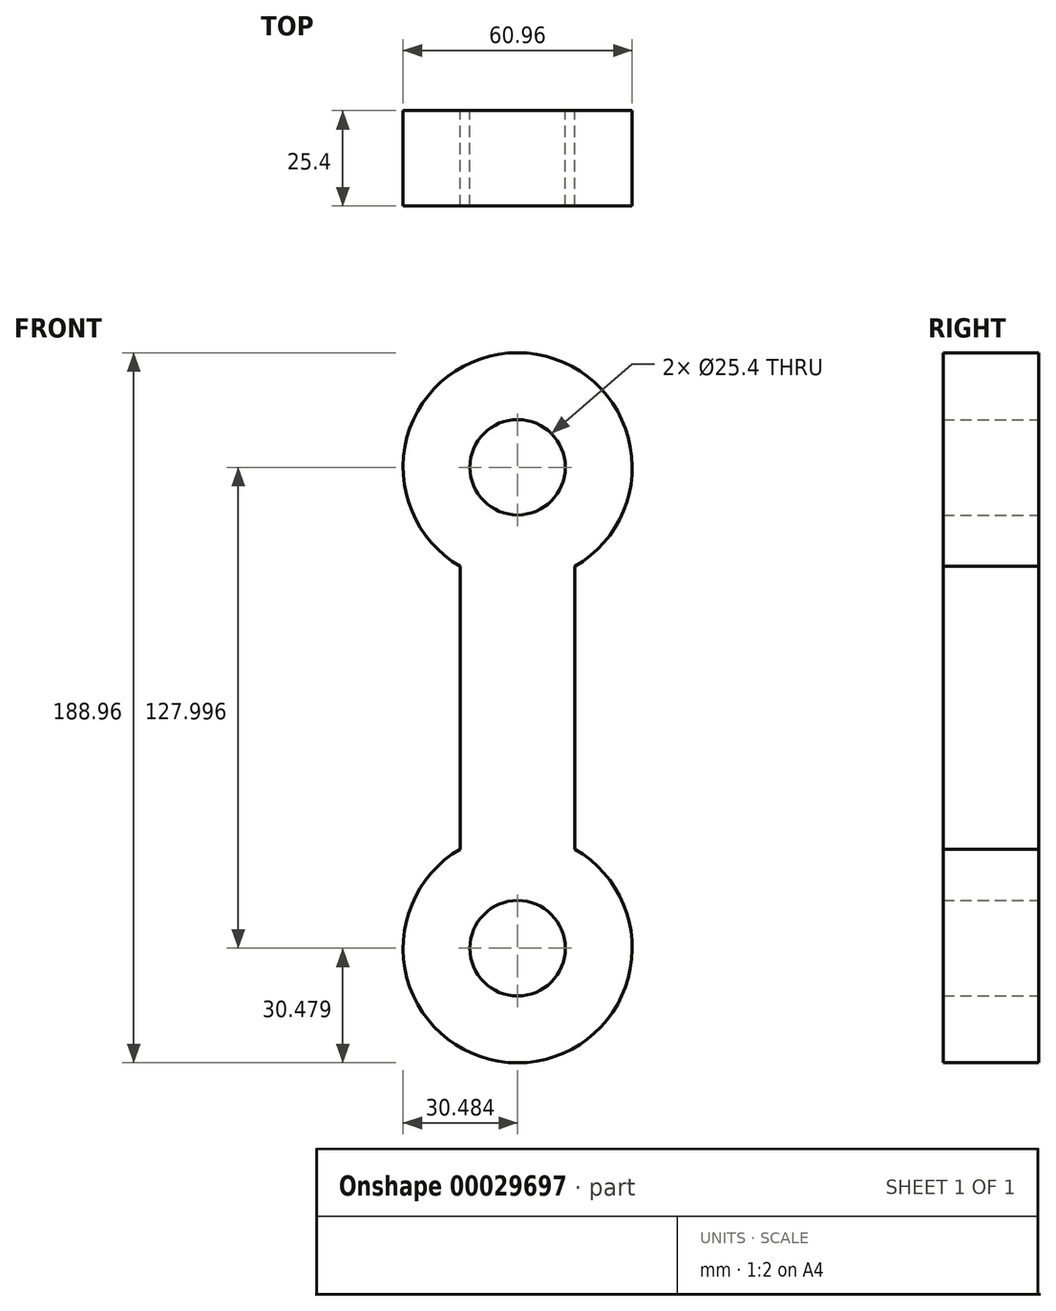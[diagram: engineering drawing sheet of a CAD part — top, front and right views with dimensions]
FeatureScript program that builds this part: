
annotation { "Feature Type Name" : "Feature", "Feature Type Description" : "" }
export const myFeature = defineFeature(function(context is Context, id is Id, definition is map)
    precondition{}
    {
        {
            var Q0;
            Q0=qCreatedBy(makeId("Front.planeOp"),FACE);
            var sketch = newSketch(context, id + "F0", { "sketchPlane" : qUnion([Q0])});
            skLineSegment(sketch, "E0.left", {"start": v(-16.98, 1.59) * mm, "end": v(-16.98, -73.61) * mm});
            skLineSegment(sketch, "E0.right", {"start": v(13.5, 1.59) * mm, "end": v(13.5, -73.61) * mm});
            skArc(sketch, "E1", {"start": v(13.5, 1.59) * mm, "mid": v(-1.74, 58.47) * mm, "end": v(-16.98, 1.59) * mm});
            skPoint(sketch, "E2.orphan", {"position": v(-16.98, 27.99) * mm});
            skPoint(sketch, "E3.orphan", {"position": v(13.5, 27.99) * mm});
            skCircle(sketch, "E4", {"center": v(-1.74, 27.99) * mm, "radius": 12.7 * mm});
            skArc(sketch, "E5", {"start": v(-16.98, -73.61) * mm, "mid": v(-1.74, -130.5) * mm, "end": v(13.5, -73.61) * mm});
            skPoint(sketch, "E6.orphan", {"position": v(13.5, -100.01) * mm});
            skPoint(sketch, "E0.top.start.orphan", {"position": v(-16.98, -100.01) * mm});
            skCircle(sketch, "E7", {"center": v(-1.74, -100.01) * mm, "radius": 12.7 * mm});
            skSolve(sketch);
        }
        {
            var Q0;
            Q0 = qSketchRegion(id + "F0", true);
            var Q1;
            Q1=makeQuery(id+"F0.imprint","IMPRINT",FACE,{"disambiguationData":[TD([[makeQuery(id+"F0.imprint","IMPRINT",EDGE,{"derivedFrom":sQuery(id+"F0.wireOp",EDGE,"E0.top")}),1.0]])]});
            extrude(context, id + "F1", {"entities" : qUnion([Q0, Q1]), "depth" : 25.4 * mm});
        }
    });
